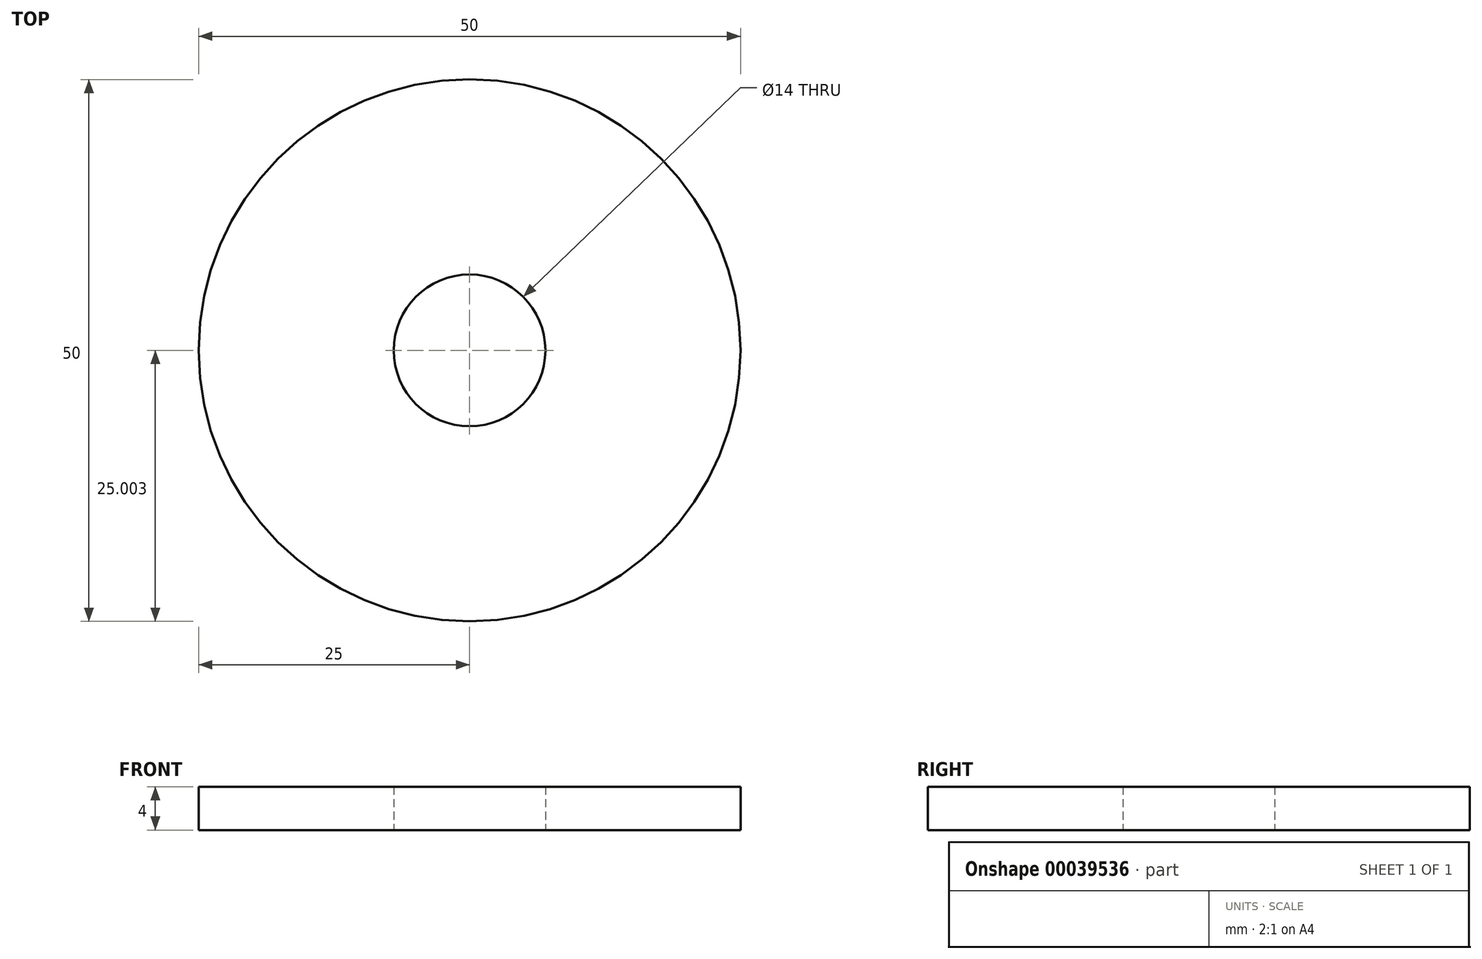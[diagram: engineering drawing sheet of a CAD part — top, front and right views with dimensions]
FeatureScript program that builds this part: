
annotation { "Feature Type Name" : "Feature", "Feature Type Description" : "" }
export const myFeature = defineFeature(function(context is Context, id is Id, definition is map)
    precondition{}
    {
        {
            var Q0;
            Q0=qCreatedBy(makeId("Top.planeOp"),FACE);
            var sketch = newSketch(context, id + "F0", { "sketchPlane" : qUnion([Q0])});
            skCircle(sketch, "E0", {"center": v(-67.66, 46.18) * mm, "radius": 25 * mm});
            skCircle(sketch, "E1", {"center": v(-67.66, 46.18) * mm, "radius": 7 * mm});
            skSolve(sketch);
        }
        {
            var Q0;
            Q0=makeQuery(id+"F0.imprint","IMPRINT",FACE,{"disambiguationData":[TD([[makeQuery(id+"F0.imprint","IMPRINT",EDGE,{"derivedFrom":sQuery(id+"F0.wireOp",EDGE,"E0")}),1.0]])]});
            extrude(context, id + "F1", {"entities" : qUnion([Q0]), "depth" : 4 * mm});
        }
    });
